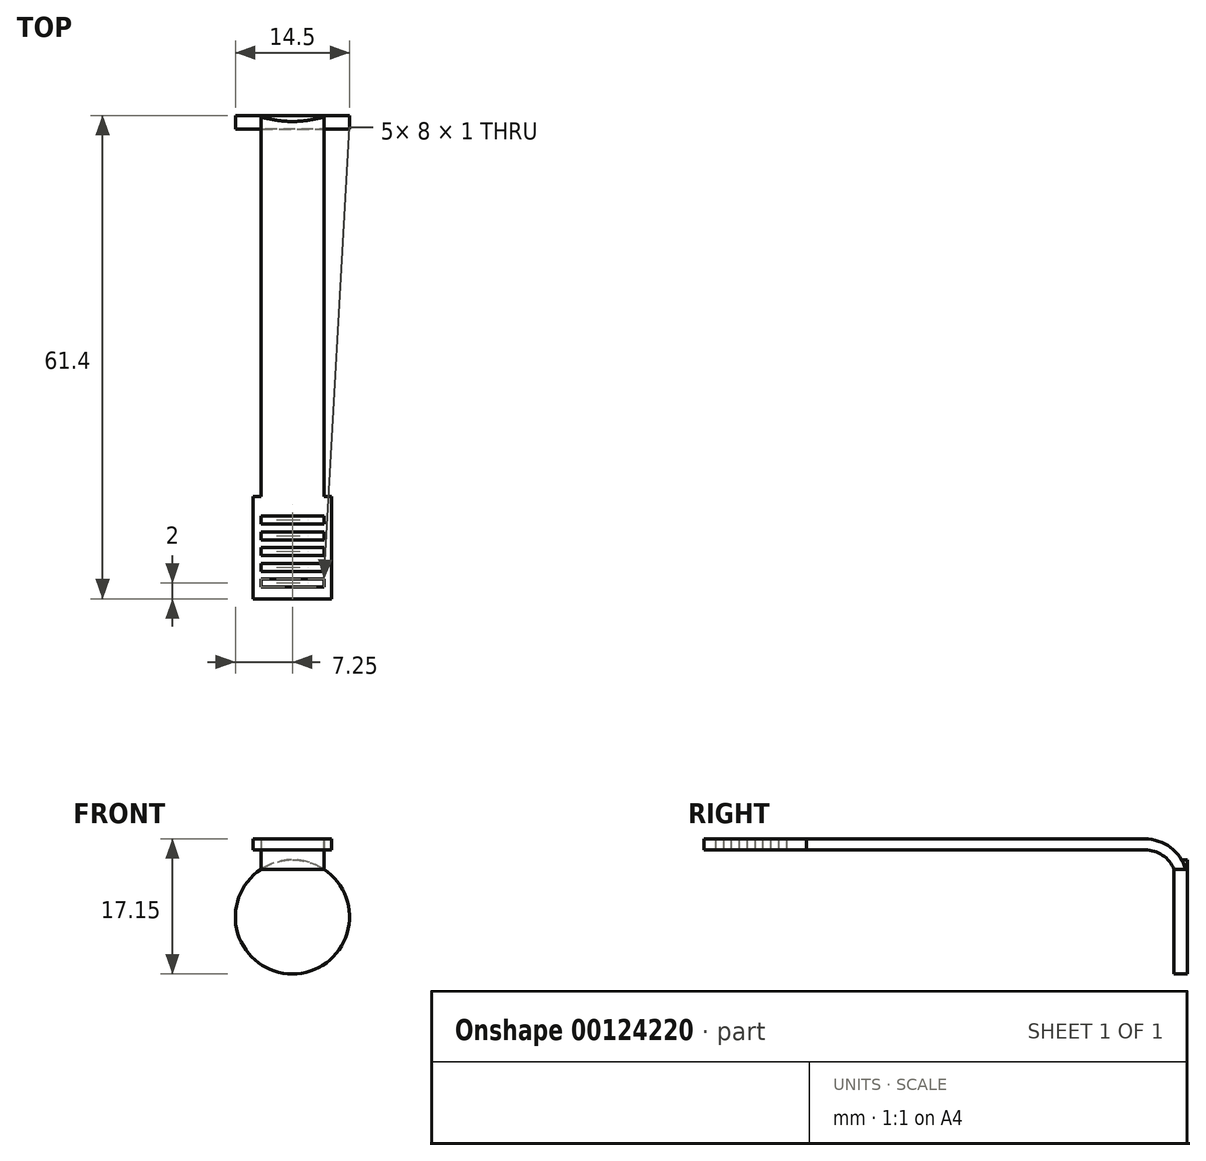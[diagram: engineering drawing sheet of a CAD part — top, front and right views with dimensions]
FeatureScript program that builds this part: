
annotation { "Feature Type Name" : "Feature", "Feature Type Description" : "" }
export const myFeature = defineFeature(function(context is Context, id is Id, definition is map)
    precondition{}
    {
        {
            var Q0;
            Q0=qCreatedBy(makeId("Top.planeOp"),FACE);
            var sketch = newSketch(context, id + "F0", { "sketchPlane" : qUnion([Q0])});
            skLineSegment(sketch, "E0.bottom", {"start": v(5, 6.5) * mm, "end": v(-5, 6.5) * mm});
            skLineSegment(sketch, "E0.top", {"start": v(5, -6.5) * mm, "end": v(-5, -6.5) * mm});
            skLineSegment(sketch, "E0.left", {"start": v(5, 6.5) * mm, "end": v(5, -6.5) * mm});
            skLineSegment(sketch, "E0.right", {"start": v(-5, 6.5) * mm, "end": v(-5, -6.5) * mm});
            skPoint(sketch, "E0.middle", {"position": v(0, 0) * mm});
            skLineSegment(sketch, "E1", {"start": v(-5, 6.5) * mm, "end": v(-4, 6.5) * mm});
            skLineSegment(sketch, "E2.bottom", {"start": v(-4, 6.5) * mm, "end": v(4, 6.5) * mm});
            skLineSegment(sketch, "E2.top", {"start": v(-4, 49.5) * mm, "end": v(4, 49.5) * mm});
            skLineSegment(sketch, "E2.left", {"start": v(-4, 6.5) * mm, "end": v(-4, 49.5) * mm});
            skLineSegment(sketch, "E2.right", {"start": v(4, 6.5) * mm, "end": v(4, 49.5) * mm});
            skLineSegment(sketch, "E3", {"start": v(4, 6.5) * mm, "end": v(5, 6.5) * mm});
            skSolve(sketch);
        }
        {
            var Q0;
            Q0=makeQuery(id+"F0.imprint","IMPRINT",FACE,{"disambiguationData":[TD([[makeQuery(id+"F0.imprint","IMPRINT",EDGE,{"derivedFrom":sQuery(id+"F0.wireOp",EDGE,"E2.bottom")}),1.0]])]});
            var Q1;
            Q1=makeQuery(id+"F0.imprint","IMPRINT",FACE,{"disambiguationData":[TD([[makeQuery(id+"F0.imprint","IMPRINT",EDGE,{"derivedFrom":sQuery(id+"F0.wireOp",EDGE,"E0.bottom")}),1.0]])]});
            var Q2;
            Q2=makeQuery(id+"F0.imprint","IMPRINT",FACE,{"disambiguationData":[TD([[makeQuery(id+"F0.imprint","IMPRINT",EDGE,{"derivedFrom":sQuery(id+"F0.wireOp",EDGE,"E0.top")}),-1.0]])]});
            var Q3;
            Q3=makeQuery(id+"F0.imprint","IMPRINT",FACE,{"disambiguationData":[TD([[makeQuery(id+"F0.imprint","IMPRINT",EDGE,{"derivedFrom":sQuery(id+"F0.wireOp",EDGE,"E2.top")}),-1.0]])]});
            extrude(context, id + "F1", {"entities" : qUnion([Q0, Q1, Q2, Q3]), "depth" : 1.4 * mm});
        }
        {
            var Q0;
            Q0=makeQuery(id+"F1.opExtrude","SWEPT_FACE",FACE,{"disambiguationData":[OSD([sQuery(id+"F0.wireOp",EDGE,"E2.right")])]});
            var sketch = newSketch(context, id + "F2", { "sketchPlane" : qUnion([Q0])});
            skLineSegment(sketch, "E4", {"start": v(49.5, 0) * mm, "end": v(49.5, 0) * mm});
            skLineSegment(sketch, "E5", {"start": v(49.5, 0) * mm, "end": v(49.5, -4) * mm, "construction": true});
            skArc(sketch, "E6", {"start": v(53.31, -5.21) * mm, "mid": v(52.73, -1.64) * mm, "end": v(49.5, 0) * mm});
            skArc(sketch, "E7", {"start": v(49.5, 1.4) * mm, "mid": v(53.32, -0.18) * mm, "end": v(54.9, -4) * mm});
            skLineSegment(sketch, "E8", {"start": v(53.31, -5.21) * mm, "end": v(54.9, -4) * mm});
            skLineSegment(sketch, "E9", {"start": v(49.5, -4) * mm, "end": v(49.5, -10.5) * mm, "construction": true});
            skLineSegment(sketch, "E10", {"start": v(-15.22, -10.5) * mm, "end": v(49.5, -10.5) * mm, "construction": true});
            skLineSegment(sketch, "E11", {"start": v(49.5, 0) * mm, "end": v(49.5, 1.4) * mm});
            skSolve(sketch);
        }
        {
            var Q0;
            {var subQ0=sQuery(id+"F2.wireOp",EDGE,"E6");Q0=makeQuery(id+"F2.imprint","IMPRINT",FACE,{"disambiguationData":[TD([[makeQuery(id+"F2.imprint","IMPRINT",EDGE,{"derivedFrom":subQ0}),-1.0]])]});}
            var Q1;
            {var subQ0=sQuery(id+"F2.wireOp",EDGE,"E11");Q1=makeQuery(id+"F2.imprint","IMPRINT",FACE,{"disambiguationData":[TD([[makeQuery(id+"F2.imprint","IMPRINT",EDGE,{"derivedFrom":subQ0}),-1.0]])]});}
            var Q2;
            Q2=makeQuery(id+"F1.opExtrude","SWEPT_FACE",FACE,{"disambiguationData":[OSD([sQuery(id+"F0.wireOp",EDGE,"E2.left")])]});
            extrude(context, id + "F3", {"entities" : qUnion([Q0, Q1]), "operationType" : NewBodyOperationType.ADD, "endBound" : BoundingType.UP_TO_SURFACE, "oppositeDirection" : true, "endBoundEntityFace" : qUnion([Q2]), "depth" : 25 * mm});
        }
        {
            var Q0;
            Q0=makeQuery(id+"F3.opExtrude","SWEPT_EDGE",EDGE,{"disambiguationData":[OSD([sQuery(id+"F2.wireOp",EDGE,"E7"),sQuery(id+"F2.wireOp",EDGE,"E8")])]});
            cPlane(context, id + "F4", {"entities" : qUnion([Q0]), "cplaneType" : CPlaneType.LINE_ANGLE, "offset" : 25 * mm, "angle" : 0 * degree, "width" : 150 * mm, "height" : 150 * mm});
        }
        {
            var Q0;
            Q0=qCreatedBy(id+"F4.planeOp",FACE);
            var sketch = newSketch(context, id + "F5", { "sketchPlane" : qUnion([Q0])});
            skLineSegment(sketch, "E12", {"start": v(0, 0) * mm, "end": v(0, -8.5) * mm, "construction": true});
            skCircle(sketch, "E13", {"center": v(0, -8.5) * mm, "radius": 7.25 * mm});
            skSolve(sketch);
        }
        {
            var Q0;
            Q0=makeQuery(id+"F5.imprint","IMPRINT",FACE,{"disambiguationData":[TD([[makeQuery(id+"F5.imprint","IMPRINT",EDGE,{"derivedFrom":sQuery(id+"F5.wireOp",EDGE,"E13")}),1.0]])]});
            extrude(context, id + "F6", {"entities" : qUnion([Q0]), "operationType" : NewBodyOperationType.ADD, "oppositeDirection" : true, "depth" : 1.7 * mm});
        }
        {
            var Q0;
            Q0=makeQuery(id+"F1.opExtrude","CAP_FACE",FACE,{"disambiguationData":[OSD([sQuery(id+"F0.wireOp",EDGE,"E0.top"),sQuery(id+"F0.wireOp",EDGE,"E0.left"),sQuery(id+"F0.wireOp",EDGE,"E0.right"),sQuery(id+"F0.wireOp",EDGE,"E2.top"),sQuery(id+"F0.wireOp",EDGE,"E2.left"),sQuery(id+"F0.wireOp",EDGE,"E2.right"),sQuery(id+"F0.wireOp",EDGE,"E0.bottom")])],"isStart":false});
            var sketch = newSketch(context, id + "F7", { "sketchPlane" : qUnion([Q0])});
            skLineSegment(sketch, "E14.bottom", {"start": v(-4, 5) * mm, "end": v(4, 5) * mm});
            skLineSegment(sketch, "E14.top", {"start": v(-4, -5) * mm, "end": v(4, -5) * mm});
            skLineSegment(sketch, "E14.left", {"start": v(-4, 5) * mm, "end": v(-4, -5) * mm});
            skLineSegment(sketch, "E14.right", {"start": v(4, 5) * mm, "end": v(4, -5) * mm});
            skPoint(sketch, "E14.middle", {"position": v(0, 0) * mm});
            skLineSegment(sketch, "E15", {"start": v(-4, -5) * mm, "end": v(-4, -4) * mm});
            skLineSegment(sketch, "E16", {"start": v(-4, -4) * mm, "end": v(4, -4) * mm});
            skLineSegment(sketch, "E17", {"start": v(4, -4) * mm, "end": v(4, -3) * mm});
            skLineSegment(sketch, "E18", {"start": v(4, -3) * mm, "end": v(-4, -3) * mm});
            skLineSegment(sketch, "E19", {"start": v(-4, -3) * mm, "end": v(-4, -2) * mm});
            skLineSegment(sketch, "E20", {"start": v(-4, -2) * mm, "end": v(4, -2) * mm});
            skLineSegment(sketch, "E21", {"start": v(4, -2) * mm, "end": v(4, -1) * mm});
            skLineSegment(sketch, "E22", {"start": v(4, -1) * mm, "end": v(-4, -1) * mm});
            skLineSegment(sketch, "E23", {"start": v(-4, -1) * mm, "end": v(-4, 0) * mm});
            skLineSegment(sketch, "E24", {"start": v(-4, 0) * mm, "end": v(4, 0) * mm});
            skLineSegment(sketch, "E25", {"start": v(4, 0) * mm, "end": v(4, 1) * mm});
            skLineSegment(sketch, "E26", {"start": v(4, 1) * mm, "end": v(-4, 1) * mm});
            skLineSegment(sketch, "E27", {"start": v(-4, 1) * mm, "end": v(-4, 2) * mm});
            skLineSegment(sketch, "E28", {"start": v(-4, 2) * mm, "end": v(4, 2) * mm});
            skLineSegment(sketch, "E29", {"start": v(4, 2) * mm, "end": v(4, 3) * mm});
            skLineSegment(sketch, "E30", {"start": v(4, 3) * mm, "end": v(-4, 3) * mm});
            skLineSegment(sketch, "E31", {"start": v(-4, 3) * mm, "end": v(-4, 4) * mm});
            skLineSegment(sketch, "E32", {"start": v(-4, 4) * mm, "end": v(4, 4) * mm});
            skSolve(sketch);
        }
        {
            var Q0;
            {var subQ0=sQuery(id+"F7.wireOp",EDGE,"E14.top");Q0=makeQuery(id+"F7.imprint","IMPRINT",FACE,{"disambiguationData":[TD([[makeQuery(id+"F7.imprint","IMPRINT",EDGE,{"derivedFrom":subQ0}),1.0]])]});}
            var Q1;
            {var subQ0=sQuery(id+"F7.wireOp",EDGE,"E18");Q1=makeQuery(id+"F7.imprint","IMPRINT",FACE,{"disambiguationData":[TD([[makeQuery(id+"F7.imprint","IMPRINT",EDGE,{"derivedFrom":subQ0}),-1.0]])]});}
            var Q2;
            {var subQ0=sQuery(id+"F7.wireOp",EDGE,"E22");Q2=makeQuery(id+"F7.imprint","IMPRINT",FACE,{"disambiguationData":[TD([[makeQuery(id+"F7.imprint","IMPRINT",EDGE,{"derivedFrom":subQ0}),-1.0]])]});}
            var Q3;
            {var subQ0=sQuery(id+"F7.wireOp",EDGE,"E26");Q3=makeQuery(id+"F7.imprint","IMPRINT",FACE,{"disambiguationData":[TD([[makeQuery(id+"F7.imprint","IMPRINT",EDGE,{"derivedFrom":subQ0}),-1.0]])]});}
            var Q4;
            {var subQ0=sQuery(id+"F7.wireOp",EDGE,"E30");Q4=makeQuery(id+"F7.imprint","IMPRINT",FACE,{"disambiguationData":[TD([[makeQuery(id+"F7.imprint","IMPRINT",EDGE,{"derivedFrom":subQ0}),-1.0]])]});}
            var Q5;
            Q5=makeQuery(id+"F1.opExtrude","CAP_FACE",FACE,{"disambiguationData":[OSD([sQuery(id+"F0.wireOp",EDGE,"E0.top"),sQuery(id+"F0.wireOp",EDGE,"E0.left"),sQuery(id+"F0.wireOp",EDGE,"E0.right"),sQuery(id+"F0.wireOp",EDGE,"E2.top"),sQuery(id+"F0.wireOp",EDGE,"E2.left"),sQuery(id+"F0.wireOp",EDGE,"E2.right"),sQuery(id+"F0.wireOp",EDGE,"E0.bottom")])],"isStart":true});
            extrude(context, id + "F8", {"entities" : qUnion([Q0, Q1, Q2, Q3, Q4]), "operationType" : NewBodyOperationType.REMOVE, "endBound" : BoundingType.UP_TO_SURFACE, "oppositeDirection" : true, "endBoundEntityFace" : qUnion([Q5]), "depth" : 25 * mm});
        }
    });
